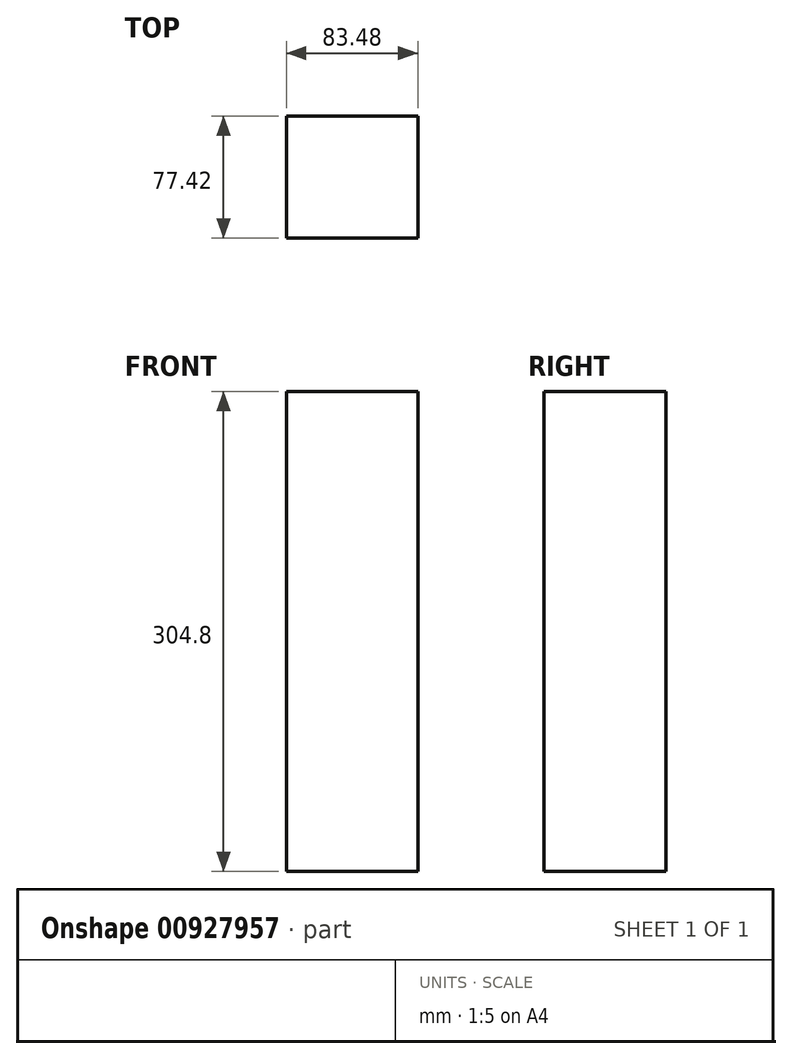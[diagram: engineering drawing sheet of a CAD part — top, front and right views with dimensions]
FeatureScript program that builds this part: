
annotation { "Feature Type Name" : "Feature", "Feature Type Description" : "" }
export const myFeature = defineFeature(function(context is Context, id is Id, definition is map)
    precondition{}
    {
        {
            var Q0;
            Q0=qCreatedBy(makeId("Top.planeOp"),FACE);
            var sketch = newSketch(context, id + "F0", { "sketchPlane" : qUnion([Q0])});
            skLineSegment(sketch, "E0.bottom", {"start": v(-41.74, 38.7) * mm, "end": v(41.74, 38.7) * mm});
            skLineSegment(sketch, "E0.top", {"start": v(-41.74, -38.7) * mm, "end": v(41.74, -38.7) * mm});
            skLineSegment(sketch, "E0.left", {"start": v(-41.74, 38.7) * mm, "end": v(-41.74, -38.7) * mm});
            skLineSegment(sketch, "E0.right", {"start": v(41.74, 38.7) * mm, "end": v(41.74, -38.7) * mm});
            skPoint(sketch, "E0.middle", {"position": v(0, 0) * mm});
            skSolve(sketch);
        }
        {
            var Q0;
            Q0 = qSketchRegion(id + "F0", true);
            extrude(context, id + "F1", {"entities" : qUnion([Q0]), "depth" : 304.8 * mm, "offsetDistance" : 25.4 * mm});
        }
    });
